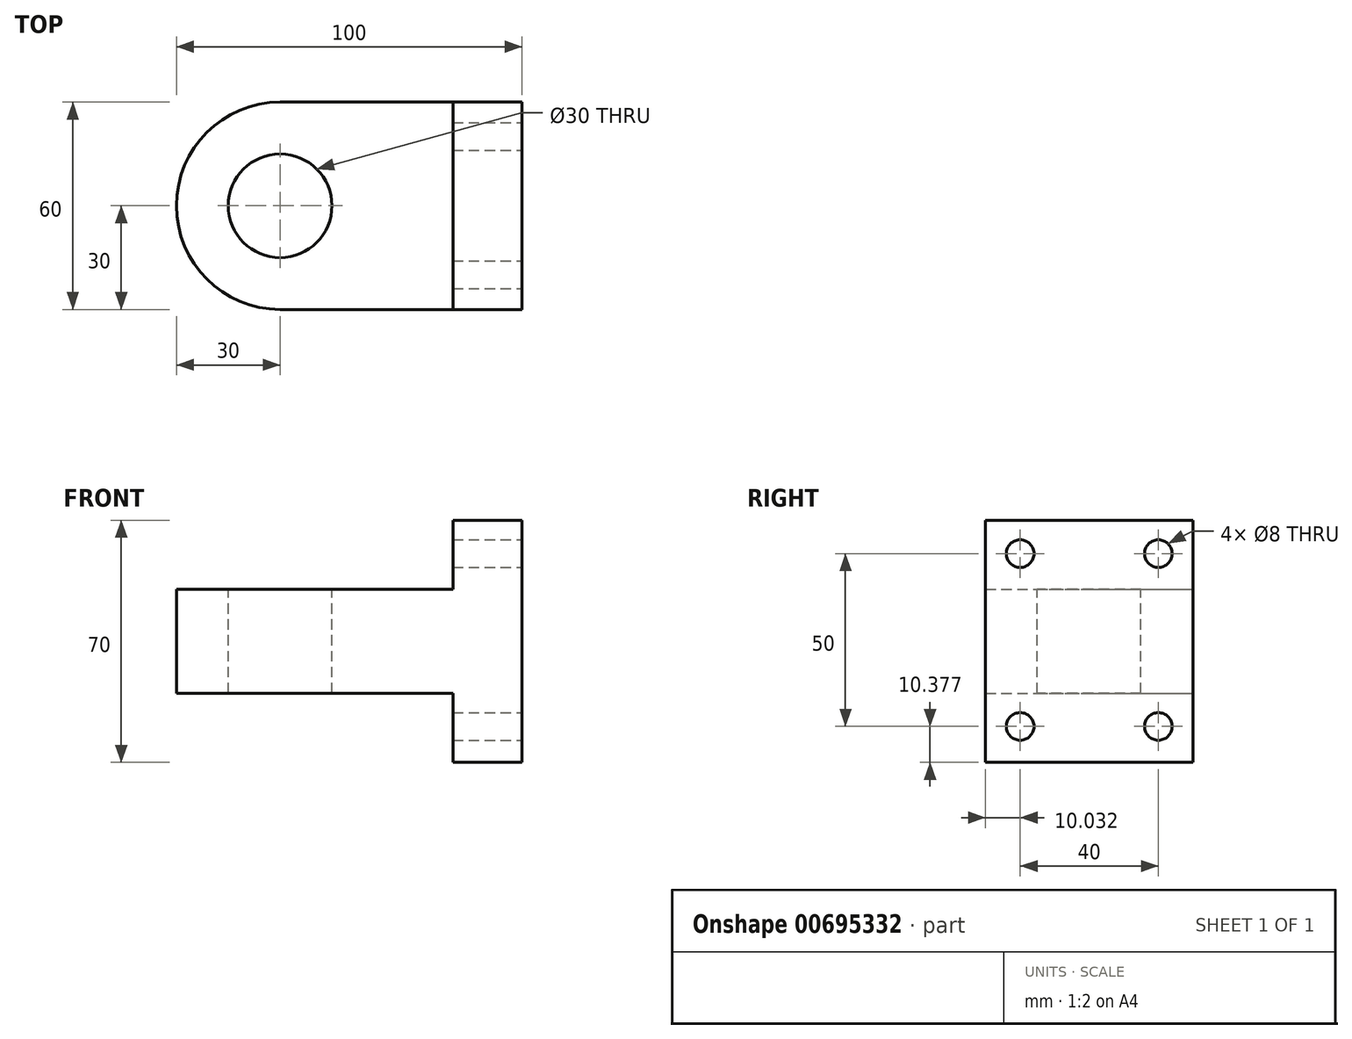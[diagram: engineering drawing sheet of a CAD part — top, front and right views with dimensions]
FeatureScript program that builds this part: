
annotation { "Feature Type Name" : "Feature", "Feature Type Description" : "" }
export const myFeature = defineFeature(function(context is Context, id is Id, definition is map)
    precondition{}
    {
        {
            var Q0;
            Q0=qCreatedBy(makeId("Front.planeOp"),FACE);
            var sketch = newSketch(context, id + "F0", { "sketchPlane" : qUnion([Q0])});
            skLineSegment(sketch, "E0", {"start": v(0, 0) * mm, "end": v(0, 35) * mm});
            skLineSegment(sketch, "E1", {"start": v(0, 35) * mm, "end": v(-20, 35) * mm});
            skLineSegment(sketch, "E2", {"start": v(-20, 35) * mm, "end": v(-20, 15) * mm});
            skLineSegment(sketch, "E3", {"start": v(-20, 15) * mm, "end": v(-100, 15) * mm});
            skLineSegment(sketch, "E4", {"start": v(-100, 15) * mm, "end": v(-100, 0) * mm});
            skLineSegment(sketch, "E5", {"start": v(-100, 0) * mm, "end": v(0, 0) * mm});
            skSolve(sketch);
        }
        {
            var Q0;
            Q0 = qSketchRegion(id + "F0", true);
            extrude(context, id + "F1", {"entities" : qUnion([Q0]), "endBound" : BoundingType.SYMMETRIC, "depth" : 60 * mm, "offsetDistance" : 25 * mm});
        }
        {
            var Q0;
            Q0=makeQuery(id+"F1.opExtrude","CAP_EDGE",EDGE,{"disambiguationData":[OSD([sQuery(id+"F0.wireOp",EDGE,"E4")])],"isStart":false});
            fillet(context, id + "F2", {"entities" : qUnion([Q0]), "radius" : 30 * mm, "tangentPropagation" : true, "allowEdgeOverflow" : false});
        }
        {
            var Q0;
            Q0=makeQuery(id+"F1.opExtrude","CAP_EDGE",EDGE,{"disambiguationData":[OSD([sQuery(id+"F0.wireOp",EDGE,"E4")])],"isStart":true});
            fillet(context, id + "F3", {"entities" : qUnion([Q0]), "radius" : 30 * mm, "tangentPropagation" : true, "allowEdgeOverflow" : false});
        }
        {
            var Q0;
            Q0=makeQuery(id+"F1.opExtrude","SWEPT_FACE",FACE,{"disambiguationData":[OSD([sQuery(id+"F0.wireOp",EDGE,"E3")])]});
            var sketch = newSketch(context, id + "F4", { "sketchPlane" : qUnion([Q0])});
            skCircle(sketch, "E6", {"center": v(-70, 0) * mm, "radius": 15 * mm});
            skSolve(sketch);
        }
        {
            var Q0;
            Q0 = qSketchRegion(id + "F4", true);
            extrude(context, id + "F5", {"entities" : qUnion([Q0]), "operationType" : NewBodyOperationType.REMOVE, "endBound" : BoundingType.UP_TO_NEXT, "oppositeDirection" : true, "depth" : 25 * mm, "offsetDistance" : 25 * mm});
        }
        {
            var Q0;
            Q0=makeQuery(id+"F1.opExtrude","SWEPT_BODY",BODY,{"disambiguationData":[OSD([sQuery(id+"F0.wireOp",EDGE,"E0"),sQuery(id+"F0.wireOp",EDGE,"E1"),sQuery(id+"F0.wireOp",EDGE,"E2"),sQuery(id+"F0.wireOp",EDGE,"E3"),sQuery(id+"F0.wireOp",EDGE,"E4"),sQuery(id+"F0.wireOp",EDGE,"E5")])]});
            var Q1;
            Q1=qCreatedBy(makeId("Top.planeOp"),FACE);
            mirror(context, id + "F6", {"operationType" : NewBodyOperationType.ADD, "entities" : qUnion([Q0]), "mirrorPlane" : qUnion([Q1])});
        }
        {
            var Q0;
            Q0=qCreatedBy(makeId("Right.planeOp"),FACE);
            var sketch = newSketch(context, id + "F7", { "sketchPlane" : qUnion([Q0])});
            skLineSegment(sketch, "E7", {"start": v(-29.97, -34.62) * mm, "end": v(-29.97, -24.62) * mm});
            skLineSegment(sketch, "E8", {"start": v(-29.97, -24.62) * mm, "end": v(-19.97, -24.62) * mm});
            skCircle(sketch, "E9", {"center": v(-19.97, -24.62) * mm, "radius": 4 * mm});
            skCircle(sketch, "E10.0.1.0", {"center": v(-19.97, 25.38) * mm, "radius": 4 * mm});
            skCircle(sketch, "E10.1.0.0", {"center": v(20.03, -24.62) * mm, "radius": 4 * mm});
            skCircle(sketch, "E10.1.1.0", {"center": v(20.03, 25.38) * mm, "radius": 4 * mm});
            skLineSegment(sketch, "E10.direction1", {"start": v(-19.97, -24.62) * mm, "end": v(20.03, -24.62) * mm, "construction": true});
            skLineSegment(sketch, "E10.direction2", {"start": v(-19.97, -24.62) * mm, "end": v(-19.97, 25.38) * mm, "construction": true});
            skSolve(sketch);
        }
        {
            var Q0;
            Q0=makeQuery(id+"F7.imprint","IMPRINT",FACE,{"disambiguationData":[TD([[makeQuery(id+"F7.imprint","IMPRINT",EDGE,{"derivedFrom":sQuery(id+"F7.wireOp",EDGE,"E10.0.1.0")}),1.0]])]});
            var Q1;
            Q1=makeQuery(id+"F7.imprint","IMPRINT",FACE,{"disambiguationData":[TD([[makeQuery(id+"F7.imprint","IMPRINT",EDGE,{"derivedFrom":sQuery(id+"F7.wireOp",EDGE,"E10.1.1.0")}),1.0]])]});
            var Q2;
            Q2=makeQuery(id+"F7.imprint","IMPRINT",FACE,{"disambiguationData":[TD([[makeQuery(id+"F7.imprint","IMPRINT",EDGE,{"derivedFrom":sQuery(id+"F7.wireOp",EDGE,"E9")}),1.0]])]});
            var Q3;
            Q3=makeQuery(id+"F7.imprint","IMPRINT",FACE,{"disambiguationData":[TD([[makeQuery(id+"F7.imprint","IMPRINT",EDGE,{"derivedFrom":sQuery(id+"F7.wireOp",EDGE,"E10.1.0.0")}),1.0]])]});
            extrude(context, id + "F8", {"entities" : qUnion([Q0, Q1, Q2, Q3]), "operationType" : NewBodyOperationType.REMOVE, "endBound" : BoundingType.UP_TO_NEXT, "oppositeDirection" : true, "depth" : 25 * mm, "offsetDistance" : 25 * mm});
        }
    });
